# Revit family: Building-RicaricaVeicoliElettrici-GEWISS-JOINON-ICON
name_source: partatom
category: Apparecchi elettrici
units: mm (PartAtom-declared; Revit-internal decimal feet)

## family parameters
Condiviso = No
Host = Superficie
Mantenere orientamento annotazione = Sì
Punto di calcolo locali = Sì
Quota connettore circolare = Usa diametro
Taglio con vuoti quando caricato = No
Tipo di parte = Normale

## types (1)
- Building-RicaricaVeicoliElettrici-GEWISS-JOINON-ICON
    Attivazione ricarica = Accesso Libero, con gestione dinamica dei carichi
    BLOCCO = B=C
    Caratteristiche meccaniche = -
    Codice Electrocod = 2242
    Colore = Grigio scuro
    Connettività: = BLE
    Contatore di energia = Attualmente non presente
    Corrente erogata (max): = 16 Ampere
    Corrente nominale: = 16 Ampere
    DC Leakage check = Si
    Descrizione = JOINON I-CON AUTOSTART DLM 11KW T2
    FORMULA = 1000 mm  [stored 3.28084 ft]
    Grado di protezione = IP55
    Human Interface = Led RGB
    IDF = 39411672-1068-4547-af07-d1586e25650a
    INPUT: = -
    Immagine tipo = ICON.jpg
    L = 155 mm  [stored 0.50853 ft]
    Materiale = Termoplastico (origine Post Industrial)
    Modello = GWJ3103A
    Morsettiera: = 5 x 10 mm²
    N. Prese Tipo 2 = 1
    N.poli = 1
    Numero di prese (tipo) = 1 (Tipo 2, con shutter)
    OUTPUT : = -
    POMELLO = bianco
    PRESA = Giallo
    Personalizzabile: = SI (frontale)
    Potenza complessiva: = 11 Chilowatt
    Potenza di ricarica = 11 kW
    Potenza max = 11 Chilowatt
    Produttore = GEWISS S.p.A.
    Prospetto di default = 1219 mm
    Protezione magnetotermica = Attualmente non presente
    Protezioni = DC Leak 6mA
    Resistenza agli urti = IK10
    Riarmo protezioni da remoto = Attualmente non presente
    STRUTTURA = RAL - 7035
    STRUTTURA ALTA = blue
    Spostamento_S = 1500 mm  [stored 4.92126 ft]
    Temperatura di utilizzo = -25 +50 °C
    Tensione nominale = 400 Volt
    Tensione nominale di isolamento (Ui) = 400 Volt
    Tipo di installazione e montaggio = A parete o su supporto a pavimento
    Tipo di protezione differenziale = Attualmente non presente
    Tipologia Presa: = Tipo 2 antivandalo con shutter
    Trattamento esterno = No
    URL = https://www.gewiss.com
    VETRO = Vetro
    Versione file RFA = 19.4
    Voltaggio = 0 V
    W = 115 mm  [stored 0.377297 ft]

note: [stored X ft] marks values corroborated as IEEE doubles in the binary element streams (Revit-internal decimal feet)

## geometry (parser evidence)
native form markers: Sweep x2
no freeform markers — native parametric forms only
